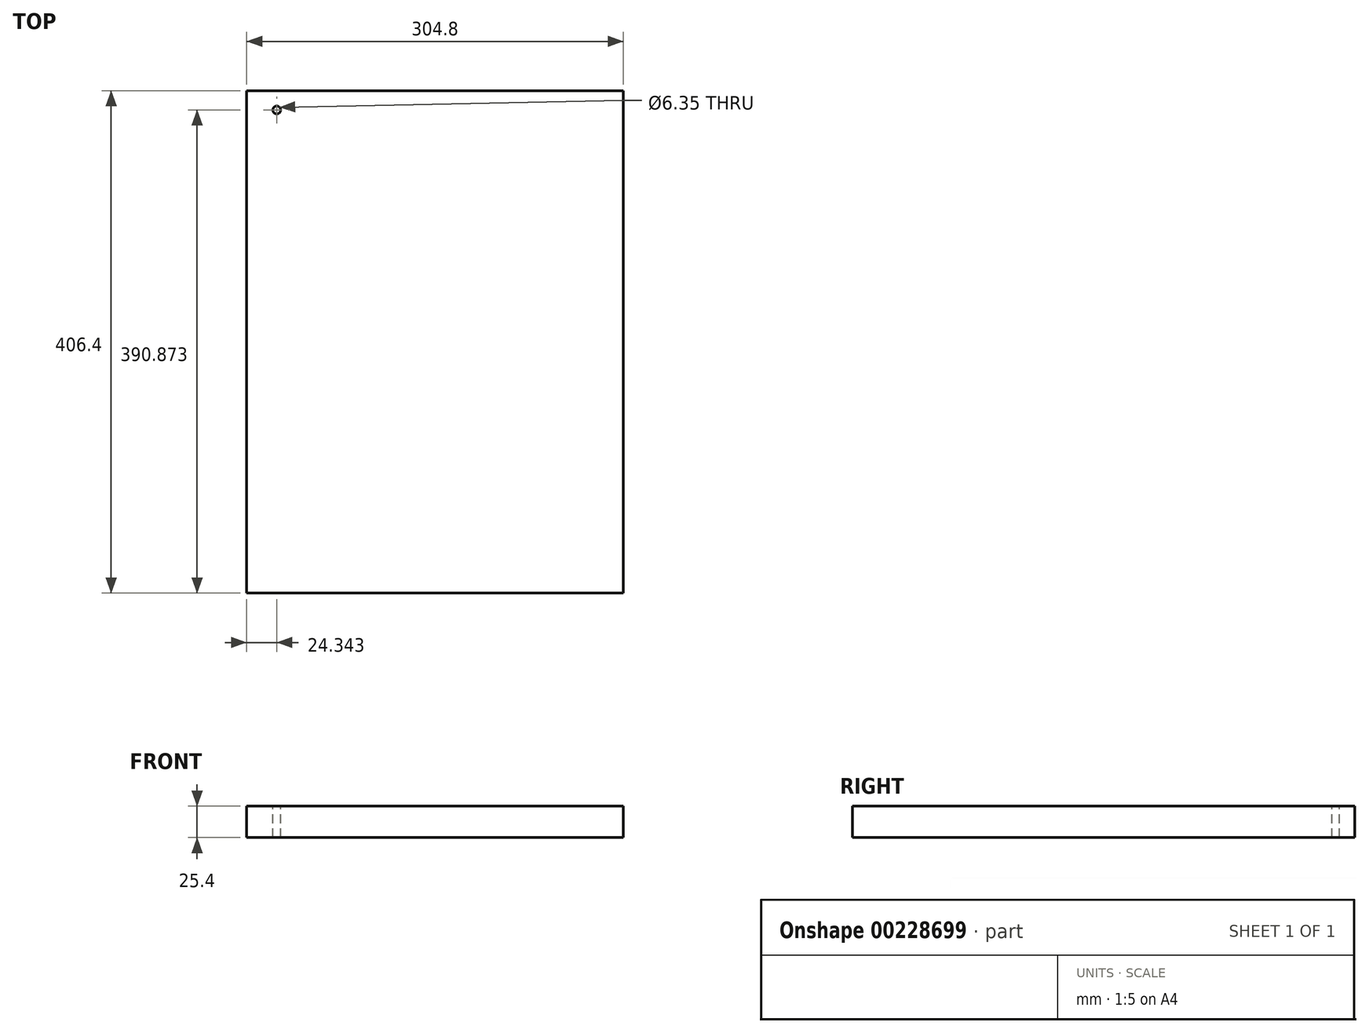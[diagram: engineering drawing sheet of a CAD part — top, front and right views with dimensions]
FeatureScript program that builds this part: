
annotation { "Feature Type Name" : "Feature", "Feature Type Description" : "" }
export const myFeature = defineFeature(function(context is Context, id is Id, definition is map)
    precondition{}
    {
        {
            var Q0;
            Q0=qCreatedBy(makeId("Top.planeOp"),FACE);
            var sketch = newSketch(context, id + "F0", { "sketchPlane" : qUnion([Q0])});
            skLineSegment(sketch, "E0.bottom", {"start": v(152.4, -203.2) * mm, "end": v(-152.4, -203.2) * mm});
            skLineSegment(sketch, "E0.top", {"start": v(152.4, 203.2) * mm, "end": v(-152.4, 203.2) * mm});
            skLineSegment(sketch, "E0.left", {"start": v(152.4, -203.2) * mm, "end": v(152.4, 203.2) * mm});
            skLineSegment(sketch, "E0.right", {"start": v(-152.4, -203.2) * mm, "end": v(-152.4, 203.2) * mm});
            skPoint(sketch, "E0.middle", {"position": v(0, 0) * mm});
            skSolve(sketch);
        }
        {
            var Q0;
            Q0 = qSketchRegion(id + "F0", true);
            extrude(context, id + "F1", {"entities" : qUnion([Q0]), "depth" : 25.4 * mm, "offsetDistance" : 25.4 * mm});
        }
        {
            var Q0;
            Q0=makeQuery(id+"F1.opExtrude","CAP_FACE",FACE,{"disambiguationData":[OSD([sQuery(id+"F0.wireOp",EDGE,"E0.bottom"),sQuery(id+"F0.wireOp",EDGE,"E0.top"),sQuery(id+"F0.wireOp",EDGE,"E0.left"),sQuery(id+"F0.wireOp",EDGE,"E0.right")])],"isStart":false});
            var sketch = newSketch(context, id + "F2", { "sketchPlane" : qUnion([Q0])});
            skPoint(sketch, "E1", {"position": v(-128.06, 187.67) * mm});
            skSolve(sketch);
        }
        {
            var Q0;
            Q0=sQuery(id+"F2.wireOp",VERTEX,"E1");
            var Q1;
            Q1=makeQuery(id+"F1.opExtrude","SWEPT_BODY",BODY,{"disambiguationData":[OSD([sQuery(id+"F0.wireOp",EDGE,"E0.bottom"),sQuery(id+"F0.wireOp",EDGE,"E0.top"),sQuery(id+"F0.wireOp",EDGE,"E0.left"),sQuery(id+"F0.wireOp",EDGE,"E0.right")])]});
            hole(context, id + "F3", {"style" : HoleStyle.SIMPLE, "endStyle" : HoleEndStyle.THROUGH, "holeDiameter" : 6.35 * mm, "majorDiameter" : 6.35 * mm, "isTappedThrough" : true, "tappedDepth" : 12.7 * mm, "tapClearance" : 3, "locations" : qUnion([Q0]), "scope" : qUnion([Q1])});
        }
    });
